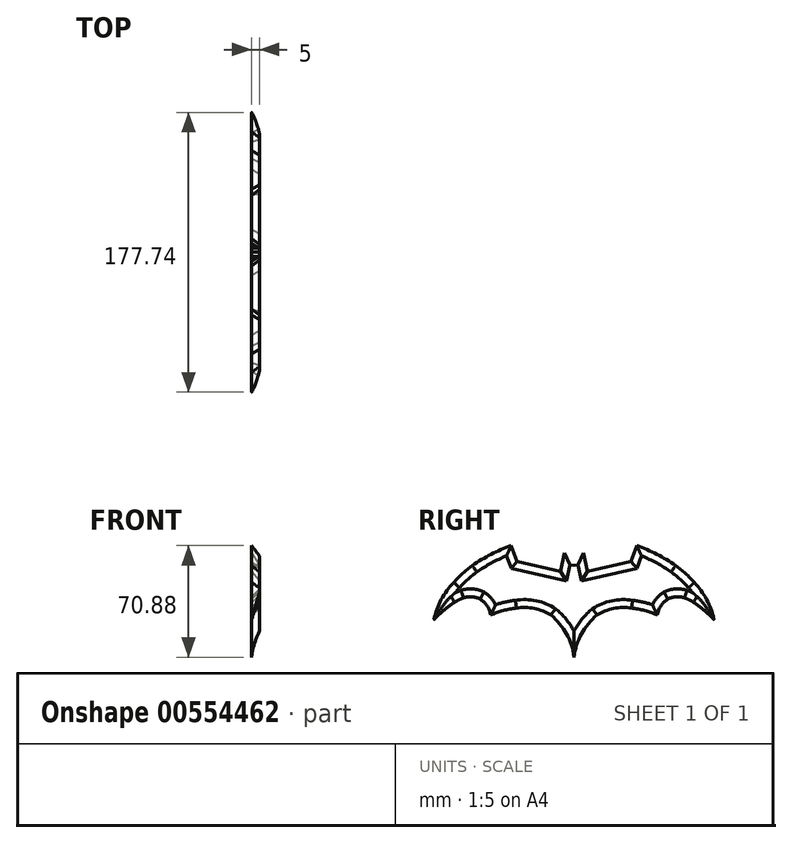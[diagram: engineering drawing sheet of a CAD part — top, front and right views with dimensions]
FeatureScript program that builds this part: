
annotation { "Feature Type Name" : "Feature", "Feature Type Description" : "" }
export const myFeature = defineFeature(function(context is Context, id is Id, definition is map)
    precondition{}
    {
        {
            var Q0;
            Q0=qCreatedBy(makeId("Right.planeOp"),FACE);
            var sketch = newSketch(context, id + "F0", { "sketchPlane" : qUnion([Q0])});
            skLineSegment(sketch, "E0", {"start": v(0, 17.79) * mm, "end": v(-2.65, 18.4) * mm});
            skLineSegment(sketch, "E1", {"start": v(-2.65, 18.4) * mm, "end": v(-5.94, 25.91) * mm});
            skLineSegment(sketch, "E2", {"start": v(-5.94, 25.91) * mm, "end": v(-8.64, 14.16) * mm});
            skLineSegment(sketch, "E3", {"start": v(-8.64, 14.16) * mm, "end": v(-36.11, 20.42) * mm});
            skLineSegment(sketch, "E4", {"start": v(-36.11, 20.42) * mm, "end": v(-39.9, 30.5) * mm});
            skLineSegment(sketch, "E5.MirrorCS", {"start": v(0, 17.79) * mm, "end": v(2.67, 18.4) * mm});
            skLineSegment(sketch, "E6.MirrorCS", {"start": v(2.67, 18.4) * mm, "end": v(5.96, 25.91) * mm});
            skLineSegment(sketch, "E7.MirrorCS", {"start": v(5.96, 25.91) * mm, "end": v(8.66, 14.16) * mm});
            skLineSegment(sketch, "E8.MirrorCS", {"start": v(8.66, 14.16) * mm, "end": v(36.13, 20.42) * mm});
            skLineSegment(sketch, "E9.MirrorCS", {"start": v(36.13, 20.42) * mm, "end": v(39.9, 30.5) * mm});
            skArc(sketch, "E10", {"start": v(-39.9, 30.5) * mm, "mid": v(-52.67, 25.02) * mm, "end": v(-64.57, 17.84) * mm});
            skArc(sketch, "E11", {"start": v(-64.57, 17.84) * mm, "mid": v(-70.75, 12.8) * mm, "end": v(-76.36, 7.11) * mm});
            skArc(sketch, "E12", {"start": v(-76.36, 7.11) * mm, "mid": v(-84.3, -3.8) * mm, "end": v(-88.9, -16.5) * mm});
            skArc(sketch, "E13", {"start": v(-85.9, -13.53) * mm, "mid": v(-87.43, -14.99) * mm, "end": v(-88.9, -16.5) * mm});
            skArc(sketch, "E14", {"start": v(-75.78, -5.41) * mm, "mid": v(-81.06, -9.2) * mm, "end": v(-85.9, -13.53) * mm});
            skArc(sketch, "E15", {"start": v(-70.15, -2.7) * mm, "mid": v(-73.06, -3.87) * mm, "end": v(-75.78, -5.41) * mm});
            skArc(sketch, "E16", {"start": v(-59.59, -3.38) * mm, "mid": v(-64.8, -1.98) * mm, "end": v(-70.15, -2.7) * mm});
            skArc(sketch, "E17", {"start": v(-52.93, -13.55) * mm, "mid": v(-55.18, -7.76) * mm, "end": v(-59.59, -3.38) * mm});
            skArc(sketch, "E18", {"start": v(-36.52, -9.17) * mm, "mid": v(-44.9, -10.74) * mm, "end": v(-52.93, -13.55) * mm});
            skArc(sketch, "E19", {"start": v(-14.65, -13.62) * mm, "mid": v(-25.18, -9.38) * mm, "end": v(-36.52, -9.17) * mm});
            skArc(sketch, "E20", {"start": v(0, -40.38) * mm, "mid": v(-4.7, -25.56) * mm, "end": v(-14.65, -13.62) * mm});
            skArc(sketch, "E21.MirrorCS", {"start": v(0, -40.38) * mm, "mid": v(4.71, -25.56) * mm, "end": v(14.67, -13.62) * mm});
            skArc(sketch, "E22.MirrorCS", {"start": v(14.67, -13.62) * mm, "mid": v(25.2, -9.38) * mm, "end": v(36.54, -9.17) * mm});
            skArc(sketch, "E23.MirrorCS", {"start": v(36.54, -9.17) * mm, "mid": v(44.9, -10.74) * mm, "end": v(52.95, -13.55) * mm});
            skArc(sketch, "E24.MirrorCS", {"start": v(52.95, -13.55) * mm, "mid": v(55.2, -7.76) * mm, "end": v(59.6, -3.38) * mm});
            skArc(sketch, "E25.MirrorCS", {"start": v(59.6, -3.38) * mm, "mid": v(64.82, -1.98) * mm, "end": v(70.17, -2.7) * mm});
            skArc(sketch, "E26.MirrorCS", {"start": v(70.17, -2.7) * mm, "mid": v(73.08, -3.87) * mm, "end": v(75.8, -5.41) * mm});
            skArc(sketch, "E27.MirrorCS", {"start": v(75.8, -5.41) * mm, "mid": v(81.08, -9.2) * mm, "end": v(85.92, -13.53) * mm});
            skArc(sketch, "E28.MirrorCS", {"start": v(85.92, -13.53) * mm, "mid": v(87.45, -14.99) * mm, "end": v(88.9, -16.5) * mm});
            skArc(sketch, "E29.MirrorCS", {"start": v(76.38, 7.11) * mm, "mid": v(84.33, -3.8) * mm, "end": v(88.9, -16.5) * mm});
            skArc(sketch, "E30.MirrorCS", {"start": v(64.59, 17.84) * mm, "mid": v(70.77, 12.8) * mm, "end": v(76.38, 7.11) * mm});
            skArc(sketch, "E31.MirrorCS", {"start": v(39.9, 30.5) * mm, "mid": v(52.69, 25.02) * mm, "end": v(64.59, 17.84) * mm});
            skLineSegment(sketch, "E32", {"start": v(-88.95, 31.5) * mm, "end": v(-88.95, -40.38) * mm});
            skLineSegment(sketch, "E33", {"start": v(88.85, 31.5) * mm, "end": v(88.85, -40.38) * mm});
            skPoint(sketch, "E34.orphan", {"position": v(88.85, -41.4) * mm});
            skPoint(sketch, "E35.orphan", {"position": v(-88.95, -41.4) * mm});
            skLineSegment(sketch, "E36", {"start": v(-88.95, -40.38) * mm, "end": v(88.85, -40.38) * mm});
            skLineSegment(sketch, "E37", {"start": v(-88.95, 30.5) * mm, "end": v(88.85, 30.5) * mm});
            skSolve(sketch);
        }
        {
            var Q0;
            Q0=makeQuery(id+"F0.imprint","IMPRINT",FACE,{"disambiguationData":[TD([[makeQuery(id+"F0.imprint","IMPRINT",EDGE,{"derivedFrom":sQuery(id+"F0.wireOp",EDGE,"E0")}),1.0]])]});
            extrude(context, id + "F1", {"entities" : qUnion([Q0]), "depth" : 5 * mm, "offsetDistance" : 25 * mm});
        }
        {
            var Q0;
            Q0=makeQuery(id+"F1.opExtrude","CAP_EDGE",EDGE,{"disambiguationData":[OSD([sQuery(id+"F0.wireOp",EDGE,"E11")])],"isStart":false});
            var Q1;
            Q1=makeQuery(id+"F1.opExtrude","CAP_EDGE",EDGE,{"disambiguationData":[OSD([sQuery(id+"F0.wireOp",EDGE,"E12")])],"isStart":false});
            var Q2;
            Q2=makeQuery(id+"F1.opExtrude","CAP_EDGE",EDGE,{"disambiguationData":[OSD([sQuery(id+"F0.wireOp",EDGE,"E10")])],"isStart":false});
            var Q3;
            Q3=makeQuery(id+"F1.opExtrude","CAP_EDGE",EDGE,{"disambiguationData":[OSD([sQuery(id+"F0.wireOp",EDGE,"E14")])],"isStart":false});
            var Q4;
            Q4=makeQuery(id+"F1.opExtrude","CAP_EDGE",EDGE,{"disambiguationData":[OSD([sQuery(id+"F0.wireOp",EDGE,"E16")])],"isStart":false});
            var Q5;
            Q5=makeQuery(id+"F1.opExtrude","CAP_EDGE",EDGE,{"disambiguationData":[OSD([sQuery(id+"F0.wireOp",EDGE,"E15")])],"isStart":false});
            var Q6;
            Q6=makeQuery(id+"F1.opExtrude","CAP_EDGE",EDGE,{"disambiguationData":[OSD([sQuery(id+"F0.wireOp",EDGE,"E17")])],"isStart":false});
            var Q7;
            Q7=makeQuery(id+"F1.opExtrude","CAP_EDGE",EDGE,{"disambiguationData":[OSD([sQuery(id+"F0.wireOp",EDGE,"E18")])],"isStart":false});
            var Q8;
            Q8=makeQuery(id+"F1.opExtrude","CAP_EDGE",EDGE,{"disambiguationData":[OSD([sQuery(id+"F0.wireOp",EDGE,"E19")])],"isStart":false});
            var Q9;
            Q9=makeQuery(id+"F1.opExtrude","CAP_EDGE",EDGE,{"disambiguationData":[OSD([sQuery(id+"F0.wireOp",EDGE,"E20")])],"isStart":false});
            var Q10;
            Q10=makeQuery(id+"F1.opExtrude","CAP_EDGE",EDGE,{"disambiguationData":[OSD([sQuery(id+"F0.wireOp",EDGE,"E21.MirrorCS")])],"isStart":false});
            var Q11;
            Q11=makeQuery(id+"F1.opExtrude","CAP_EDGE",EDGE,{"disambiguationData":[OSD([sQuery(id+"F0.wireOp",EDGE,"E22.MirrorCS")])],"isStart":false});
            var Q12;
            Q12=makeQuery(id+"F1.opExtrude","CAP_EDGE",EDGE,{"disambiguationData":[OSD([sQuery(id+"F0.wireOp",EDGE,"E23.MirrorCS")])],"isStart":false});
            var Q13;
            Q13=makeQuery(id+"F1.opExtrude","CAP_EDGE",EDGE,{"disambiguationData":[OSD([sQuery(id+"F0.wireOp",EDGE,"E24.MirrorCS")])],"isStart":false});
            var Q14;
            Q14=makeQuery(id+"F1.opExtrude","CAP_EDGE",EDGE,{"disambiguationData":[OSD([sQuery(id+"F0.wireOp",EDGE,"E25.MirrorCS")])],"isStart":false});
            var Q15;
            Q15=makeQuery(id+"F1.opExtrude","CAP_EDGE",EDGE,{"disambiguationData":[OSD([sQuery(id+"F0.wireOp",EDGE,"E26.MirrorCS")])],"isStart":false});
            var Q16;
            Q16=makeQuery(id+"F1.opExtrude","CAP_EDGE",EDGE,{"disambiguationData":[OSD([sQuery(id+"F0.wireOp",EDGE,"E27.MirrorCS")])],"isStart":false});
            var Q17;
            Q17=makeQuery(id+"F1.opExtrude","CAP_EDGE",EDGE,{"disambiguationData":[OSD([sQuery(id+"F0.wireOp",EDGE,"E29.MirrorCS")])],"isStart":false});
            var Q18;
            Q18=makeQuery(id+"F1.opExtrude","CAP_EDGE",EDGE,{"disambiguationData":[OSD([sQuery(id+"F0.wireOp",EDGE,"E30.MirrorCS")])],"isStart":false});
            var Q19;
            Q19=makeQuery(id+"F1.opExtrude","CAP_EDGE",EDGE,{"disambiguationData":[OSD([sQuery(id+"F0.wireOp",EDGE,"E31.MirrorCS")])],"isStart":false});
            var Q20;
            Q20=makeQuery(id+"F1.opExtrude","CAP_EDGE",EDGE,{"disambiguationData":[OSD([sQuery(id+"F0.wireOp",EDGE,"E9.MirrorCS")])],"isStart":false});
            var Q21;
            Q21=makeQuery(id+"F1.opExtrude","CAP_EDGE",EDGE,{"disambiguationData":[OSD([sQuery(id+"F0.wireOp",EDGE,"E8.MirrorCS")])],"isStart":false});
            var Q22;
            Q22=makeQuery(id+"F1.opExtrude","CAP_EDGE",EDGE,{"disambiguationData":[OSD([sQuery(id+"F0.wireOp",EDGE,"E7.MirrorCS")])],"isStart":false});
            var Q23;
            Q23=makeQuery(id+"F1.opExtrude","CAP_EDGE",EDGE,{"disambiguationData":[OSD([sQuery(id+"F0.wireOp",EDGE,"E2")])],"isStart":false});
            var Q24;
            Q24=makeQuery(id+"F1.opExtrude","CAP_EDGE",EDGE,{"disambiguationData":[OSD([sQuery(id+"F0.wireOp",EDGE,"E3")])],"isStart":false});
            var Q25;
            Q25=makeQuery(id+"F1.opExtrude","CAP_EDGE",EDGE,{"disambiguationData":[OSD([sQuery(id+"F0.wireOp",EDGE,"E4")])],"isStart":false});
            chamfer(context, id + "F2", {"entities" : qUnion([Q0, Q1, Q2, Q3, Q4, Q5, Q6, Q7, Q8, Q9, Q10, Q11, Q12, Q13, Q14, Q15, Q16, Q17, Q18, Q19, Q20, Q21, Q22, Q23, Q24, Q25]), "width" : 5 * mm, "tangentPropagation" : true});
        }
    });
